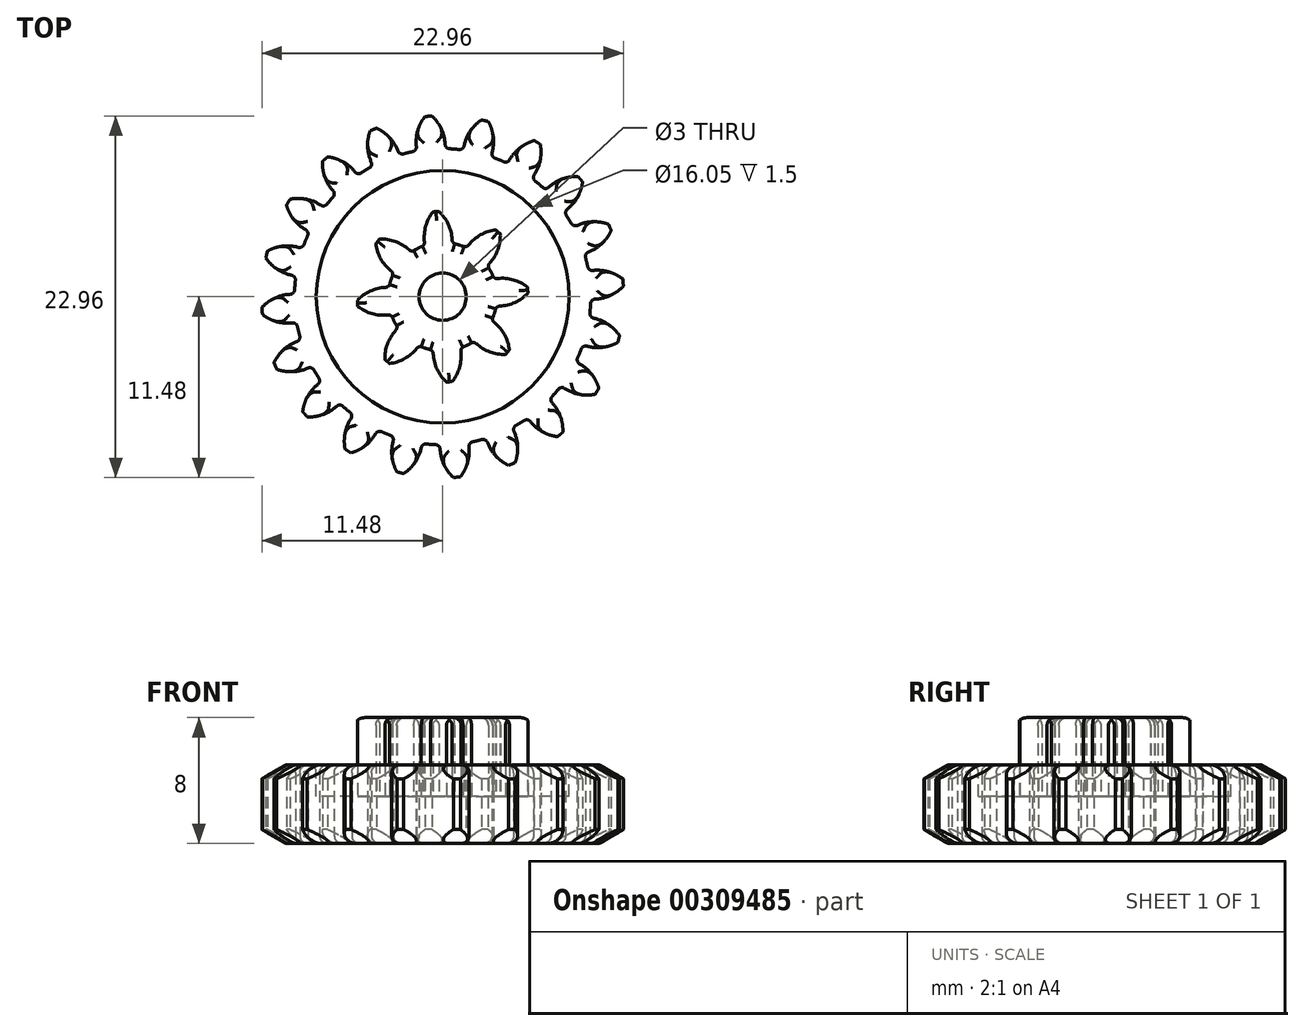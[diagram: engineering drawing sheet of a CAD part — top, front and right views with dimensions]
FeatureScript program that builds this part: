
annotation { "Feature Type Name" : "Feature", "Feature Type Description" : "" }
export const myFeature = defineFeature(function(context is Context, id is Id, definition is map)
    precondition{}
    {
        {
            assignVariable(context, id + "F0", {"name" : "GearDepth", "anyValue" : 5});
        }
        {
            var Q0;
            Q0=qCreatedBy(makeId("Top.planeOp"),FACE);
            var sketch = newSketch(context, id + "F1", { "sketchPlane" : qUnion([Q0])});
            skArc(sketch, "E0", {"start": v(-1.9, 9.21) * mm, "mid": v(0.74, -9.38) * mm, "end": v(0.44, 9.4) * mm});
            skCircle(sketch, "E1", {"center": v(0, 0) * mm, "radius": 10.45 * mm, "construction": true});
            skCircle(sketch, "E2", {"center": v(0, 0) * mm, "radius": 11.5 * mm, "construction": true});
            skLineSegment(sketch, "E3", {"start": v(0, 0) * mm, "end": v(0, 17.6) * mm, "construction": true});
            skLineSegment(sketch, "E4", {"start": v(0, 0) * mm, "end": v(-1.42, 18) * mm});
            skLineSegment(sketch, "E5", {"start": v(0, 10.45) * mm, "end": v(-10.54, 10.45) * mm, "construction": true});
            skLineSegment(sketch, "E6", {"start": v(0, 10.45) * mm, "end": v(-10.3, 6.7) * mm, "construction": true});
            skCircle(sketch, "E7", {"center": v(0, 10.45) * mm, "radius": 2.61 * mm, "construction": true});
            skCircle(sketch, "E8", {"center": v(-2.46, 9.56) * mm, "radius": 2.61 * mm, "construction": true});
            skArc(sketch, "E9", {"start": v(-4.91, 10.45) * mm, "mid": v(-4.92, 10.42) * mm, "end": v(-4.94, 10.39) * mm});
            skArc(sketch, "E10.trimOffspring", {"start": v(0.15, 9.68) * mm, "mid": v(-0.09, 10.66) * mm, "end": v(-0.68, 11.48) * mm});
            skArc(sketch, "E11.MirrorCS", {"start": v(-1.67, 9.54) * mm, "mid": v(-1.58, 10.55) * mm, "end": v(-1.12, 11.45) * mm});
            skLineSegment(sketch, "E12", {"start": v(-1.12, 11.45) * mm, "end": v(-0.68, 11.48) * mm});
            skCircle(sketch, "E13", {"center": v(0, 0) * mm, "radius": 1.5 * mm});
            skPoint(sketch, "E14.visualSharp", {"position": v(-1.62, 9.27) * mm});
            skArc(sketch, "E14.filletArc", {"start": v(-1.9, 9.21) * mm, "mid": v(-1.72, 9.33) * mm, "end": v(-1.67, 9.54) * mm});
            skPoint(sketch, "E15.visualSharp", {"position": v(0.15, 9.4) * mm});
            skArc(sketch, "E15.filletArc", {"start": v(0.15, 9.68) * mm, "mid": v(0.24, 9.49) * mm, "end": v(0.44, 9.4) * mm});
            skSolve(sketch);
        }
        {
            var Q0;
            {var subQ0=sQuery(id+"F1.wireOp",EDGE,"E10.trimOffspring");Q0=makeQuery(id+"F1.imprint","IMPRINT",FACE,{"disambiguationData":[TD([[makeQuery(id+"F1.imprint","IMPRINT",EDGE,{"derivedFrom":subQ0}),1.0]])]});}
            var Q1;
            {var subQ0=sQuery(id+"F1.wireOp",EDGE,"E0");var subQ1=makeQuery(id+"F1.imprint","INTERSECT",VERTEX,{"derivedFrom":[subQ0,sQuery(id+"F1.wireOp",EDGE,"E10.trimOffspring")]});Q1=makeQuery(id+"F1.imprint","IMPRINT",FACE,{"disambiguationData":[TD([[makeQuery(id+"F1.imprint","IMPRINT",EDGE,{"disambiguationData":[TD([[subQ1,-1.0]])],"derivedFrom":subQ0}),1.0]])]});}
            var Q2;
            {var subQ0=sQuery(id+"F1.wireOp",EDGE,"ff0f1e59-5a19-46eb-ac47-c6f22bc8a670.1.0");Q2=makeQuery(id+"F1.imprint","IMPRINT",FACE,{"disambiguationData":[TD([[makeQuery(id+"F1.imprint","IMPRINT",EDGE,{"derivedFrom":subQ0}),1.0]])]});}
            var Q3;
            {var subQ0=sQuery(id+"F1.wireOp",EDGE,"ff0f1e59-5a19-46eb-ac47-c6f22bc8a670.2.0");Q3=makeQuery(id+"F1.imprint","IMPRINT",FACE,{"disambiguationData":[TD([[makeQuery(id+"F1.imprint","IMPRINT",EDGE,{"derivedFrom":subQ0}),1.0]])]});}
            var Q4;
            {var subQ0=sQuery(id+"F1.wireOp",EDGE,"ff0f1e59-5a19-46eb-ac47-c6f22bc8a670.3.0");Q4=makeQuery(id+"F1.imprint","IMPRINT",FACE,{"disambiguationData":[TD([[makeQuery(id+"F1.imprint","IMPRINT",EDGE,{"derivedFrom":subQ0}),1.0]])]});}
            var Q5;
            {var subQ0=sQuery(id+"F1.wireOp",EDGE,"ff0f1e59-5a19-46eb-ac47-c6f22bc8a670.4.0");Q5=makeQuery(id+"F1.imprint","IMPRINT",FACE,{"disambiguationData":[TD([[makeQuery(id+"F1.imprint","IMPRINT",EDGE,{"derivedFrom":subQ0}),1.0]])]});}
            var Q6;
            {var subQ0=sQuery(id+"F1.wireOp",EDGE,"ff0f1e59-5a19-46eb-ac47-c6f22bc8a670.5.0");Q6=makeQuery(id+"F1.imprint","IMPRINT",FACE,{"disambiguationData":[TD([[makeQuery(id+"F1.imprint","IMPRINT",EDGE,{"derivedFrom":subQ0}),1.0]])]});}
            var Q7;
            {var subQ0=sQuery(id+"F1.wireOp",EDGE,"ff0f1e59-5a19-46eb-ac47-c6f22bc8a670.6.0");Q7=makeQuery(id+"F1.imprint","IMPRINT",FACE,{"disambiguationData":[TD([[makeQuery(id+"F1.imprint","IMPRINT",EDGE,{"derivedFrom":subQ0}),1.0]])]});}
            var Q8;
            {var subQ0=sQuery(id+"F1.wireOp",EDGE,"ff0f1e59-5a19-46eb-ac47-c6f22bc8a670.7.0");Q8=makeQuery(id+"F1.imprint","IMPRINT",FACE,{"disambiguationData":[TD([[makeQuery(id+"F1.imprint","IMPRINT",EDGE,{"derivedFrom":subQ0}),1.0]])]});}
            var Q9;
            {var subQ0=sQuery(id+"F1.wireOp",EDGE,"ff0f1e59-5a19-46eb-ac47-c6f22bc8a670.8.0");Q9=makeQuery(id+"F1.imprint","IMPRINT",FACE,{"disambiguationData":[TD([[makeQuery(id+"F1.imprint","IMPRINT",EDGE,{"derivedFrom":subQ0}),1.0]])]});}
            var Q10;
            {var subQ0=sQuery(id+"F1.wireOp",EDGE,"ff0f1e59-5a19-46eb-ac47-c6f22bc8a670.9.0");Q10=makeQuery(id+"F1.imprint","IMPRINT",FACE,{"disambiguationData":[TD([[makeQuery(id+"F1.imprint","IMPRINT",EDGE,{"derivedFrom":subQ0}),1.0]])]});}
            var Q11;
            {var subQ0=sQuery(id+"F1.wireOp",EDGE,"ff0f1e59-5a19-46eb-ac47-c6f22bc8a670.10.0");Q11=makeQuery(id+"F1.imprint","IMPRINT",FACE,{"disambiguationData":[TD([[makeQuery(id+"F1.imprint","IMPRINT",EDGE,{"derivedFrom":subQ0}),1.0]])]});}
            var Q12;
            {var subQ0=sQuery(id+"F1.wireOp",EDGE,"ff0f1e59-5a19-46eb-ac47-c6f22bc8a670.11.0");Q12=makeQuery(id+"F1.imprint","IMPRINT",FACE,{"disambiguationData":[TD([[makeQuery(id+"F1.imprint","IMPRINT",EDGE,{"derivedFrom":subQ0}),1.0]])]});}
            var Q13;
            {var subQ0=sQuery(id+"F1.wireOp",EDGE,"ff0f1e59-5a19-46eb-ac47-c6f22bc8a670.12.0");Q13=makeQuery(id+"F1.imprint","IMPRINT",FACE,{"disambiguationData":[TD([[makeQuery(id+"F1.imprint","IMPRINT",EDGE,{"derivedFrom":subQ0}),1.0]])]});}
            var Q14;
            {var subQ0=sQuery(id+"F1.wireOp",EDGE,"ff0f1e59-5a19-46eb-ac47-c6f22bc8a670.13.0");Q14=makeQuery(id+"F1.imprint","IMPRINT",FACE,{"disambiguationData":[TD([[makeQuery(id+"F1.imprint","IMPRINT",EDGE,{"derivedFrom":subQ0}),1.0]])]});}
            var Q15;
            {var subQ0=sQuery(id+"F1.wireOp",EDGE,"ff0f1e59-5a19-46eb-ac47-c6f22bc8a670.14.0");Q15=makeQuery(id+"F1.imprint","IMPRINT",FACE,{"disambiguationData":[TD([[makeQuery(id+"F1.imprint","IMPRINT",EDGE,{"derivedFrom":subQ0}),1.0]])]});}
            var Q16;
            {var subQ0=sQuery(id+"F1.wireOp",EDGE,"ff0f1e59-5a19-46eb-ac47-c6f22bc8a670.15.0");Q16=makeQuery(id+"F1.imprint","IMPRINT",FACE,{"disambiguationData":[TD([[makeQuery(id+"F1.imprint","IMPRINT",EDGE,{"derivedFrom":subQ0}),1.0]])]});}
            var Q17;
            {var subQ0=sQuery(id+"F1.wireOp",EDGE,"ff0f1e59-5a19-46eb-ac47-c6f22bc8a670.16.0");Q17=makeQuery(id+"F1.imprint","IMPRINT",FACE,{"disambiguationData":[TD([[makeQuery(id+"F1.imprint","IMPRINT",EDGE,{"derivedFrom":subQ0}),1.0]])]});}
            var Q18;
            {var subQ0=sQuery(id+"F1.wireOp",EDGE,"ff0f1e59-5a19-46eb-ac47-c6f22bc8a670.17.0");Q18=makeQuery(id+"F1.imprint","IMPRINT",FACE,{"disambiguationData":[TD([[makeQuery(id+"F1.imprint","IMPRINT",EDGE,{"derivedFrom":subQ0}),1.0]])]});}
            var Q19;
            {var subQ0=sQuery(id+"F1.wireOp",EDGE,"ff0f1e59-5a19-46eb-ac47-c6f22bc8a670.18.0");Q19=makeQuery(id+"F1.imprint","IMPRINT",FACE,{"disambiguationData":[TD([[makeQuery(id+"F1.imprint","IMPRINT",EDGE,{"derivedFrom":subQ0}),1.0]])]});}
            var Q20;
            {var subQ0=sQuery(id+"F1.wireOp",EDGE,"ff0f1e59-5a19-46eb-ac47-c6f22bc8a670.19.0");Q20=makeQuery(id+"F1.imprint","IMPRINT",FACE,{"disambiguationData":[TD([[makeQuery(id+"F1.imprint","IMPRINT",EDGE,{"derivedFrom":subQ0}),1.0]])]});}
            var Q21;
            Q21=sQuery(id+"F1.wireOp",EDGE,"E0");
            var Q22;
            Q22=sQuery(id+"F1.wireOp",EDGE,"E10.trimOffspring");
            var Q23;
            Q23=sQuery(id+"F1.wireOp",EDGE,"E12");
            var Q24;
            Q24=sQuery(id+"F1.wireOp",EDGE,"E11.MirrorCS");
            extrude(context, id + "F2", {"entities" : qUnion([Q0, Q1, Q2, Q3, Q4, Q5, Q6, Q7, Q8, Q9, Q10, Q11, Q12, Q13, Q14, Q15, Q16, Q17, Q18, Q19, Q20]), "surfaceEntities" : qUnion([Q21, Q22, Q23, Q24]), "depth" : (getVariable(context, 'GearDepth')) * mm});
        }
        {
            var Q0;
            Q0=makeQuery(id+"F2.opExtrude","SWEPT_BODY",BODY,{"disambiguationData":[OSD([sQuery(id+"F1.wireOp",EDGE,"E0"),sQuery(id+"F1.wireOp",EDGE,"E10.trimOffspring"),sQuery(id+"F1.wireOp",EDGE,"E11.MirrorCS"),sQuery(id+"F1.wireOp",EDGE,"E12"),sQuery(id+"F1.wireOp",EDGE,"E13"),sQuery(id+"F1.wireOp",EDGE,"E14.filletArc"),sQuery(id+"F1.wireOp",EDGE,"E15.filletArc")])]});
            var Q1;
            Q1=makeQuery(id+"F2.opExtrude","CAP_EDGE",EDGE,{"disambiguationData":[OSD([sQuery(id+"F1.wireOp",EDGE,"E13")])],"isStart":true});
            circularPattern(context, id + "F3", {"operationType" : NewBodyOperationType.ADD, "entities" : qUnion([Q0]), "axis" : qUnion([Q1]), "angle" : 360 * degree, "instanceCount" : 20, "equalSpace" : true});
        }
        {
            var Q0;
            Q0=qCreatedBy(makeId("Front.planeOp"),FACE);
            var sketch = newSketch(context, id + "F4", { "sketchPlane" : qUnion([Q0])});
            skLineSegment(sketch, "E16.0", {"start": v(11.48, 5) * mm, "end": v(11.48, 0) * mm});
            skLineSegment(sketch, "E17", {"start": v(11.48, 2.5) * mm, "end": v(14.42, 2.5) * mm, "construction": true});
            skLineSegment(sketch, "E18", {"start": v(8.27, 5.98) * mm, "end": v(12.07, 5.98) * mm});
            skLineSegment(sketch, "E19", {"start": v(12.07, 5.98) * mm, "end": v(12.07, 3.78) * mm});
            skLineSegment(sketch, "E20", {"start": v(12.07, 3.78) * mm, "end": v(8.27, 5.98) * mm});
            skLineSegment(sketch, "E21.MirrorCS", {"start": v(11.48, 0) * mm, "end": v(11.48, 5) * mm});
            skLineSegment(sketch, "E22.MirrorCS", {"start": v(8.27, -0.98) * mm, "end": v(12.07, -0.98) * mm});
            skLineSegment(sketch, "E23.MirrorCS", {"start": v(12.07, 1.22) * mm, "end": v(8.27, -0.98) * mm});
            skLineSegment(sketch, "E24.MirrorCS", {"start": v(12.07, -0.98) * mm, "end": v(12.07, 1.22) * mm});
            skSolve(sketch);
        }
        {
            var Q0;
            {var subQ0=sQuery(id+"F4.wireOp",EDGE,"E18");Q0=makeQuery(id+"F4.imprint","IMPRINT",FACE,{"disambiguationData":[TD([[makeQuery(id+"F4.imprint","IMPRINT",EDGE,{"derivedFrom":subQ0}),-1.0]])]});}
            var Q1;
            {var subQ0=sQuery(id+"F4.wireOp",EDGE,"E22.MirrorCS");Q1=makeQuery(id+"F4.imprint","IMPRINT",FACE,{"disambiguationData":[TD([[makeQuery(id+"F4.imprint","IMPRINT",EDGE,{"derivedFrom":subQ0}),1.0]])]});}
            var Q2;
            Q2=makeQuery(id+"F2.opExtrude","CAP_EDGE",EDGE,{"disambiguationData":[OSD([sQuery(id+"F1.wireOp",EDGE,"E13")])],"isStart":false});
            revolve(context, id + "F5", {"operationType" : NewBodyOperationType.REMOVE, "entities" : qUnion([Q0, Q1]), "axis" : qUnion([Q2]), "revolveType" : RevolveType.FULL, "oppositeDirection" : true});
        }
        {
            var Q0;
            {var subQ0=makeQuery(id+"F2.opExtrude","CAP_FACE",FACE,{"disambiguationData":[OSD([sQuery(id+"F1.wireOp",EDGE,"E0"),sQuery(id+"F1.wireOp",EDGE,"E10.trimOffspring"),sQuery(id+"F1.wireOp",EDGE,"E11.MirrorCS"),sQuery(id+"F1.wireOp",EDGE,"E12"),sQuery(id+"F1.wireOp",EDGE,"E13"),sQuery(id+"F1.wireOp",EDGE,"E14.filletArc"),sQuery(id+"F1.wireOp",EDGE,"E15.filletArc")])],"isStart":false});Q0=makeQuery(id+"F3.boolean.opBoolean","MERGE",FACE,{"derivedFrom":[subQ0,makeQuery(id+"F3.opPattern","COPY",FACE,{"derivedFrom":subQ0,"instanceName":"1"}),makeQuery(id+"F3.opPattern","COPY",FACE,{"derivedFrom":subQ0,"instanceName":"2"}),makeQuery(id+"F3.opPattern","COPY",FACE,{"derivedFrom":subQ0,"instanceName":"3"}),makeQuery(id+"F3.opPattern","COPY",FACE,{"derivedFrom":subQ0,"instanceName":"4"}),makeQuery(id+"F3.opPattern","COPY",FACE,{"derivedFrom":subQ0,"instanceName":"5"}),makeQuery(id+"F3.opPattern","COPY",FACE,{"derivedFrom":subQ0,"instanceName":"6"}),makeQuery(id+"F3.opPattern","COPY",FACE,{"derivedFrom":subQ0,"instanceName":"7"}),makeQuery(id+"F3.opPattern","COPY",FACE,{"derivedFrom":subQ0,"instanceName":"8"}),makeQuery(id+"F3.opPattern","COPY",FACE,{"derivedFrom":subQ0,"instanceName":"9"}),makeQuery(id+"F3.opPattern","COPY",FACE,{"derivedFrom":subQ0,"instanceName":"10"}),makeQuery(id+"F3.opPattern","COPY",FACE,{"derivedFrom":subQ0,"instanceName":"11"}),makeQuery(id+"F3.opPattern","COPY",FACE,{"derivedFrom":subQ0,"instanceName":"12"}),makeQuery(id+"F3.opPattern","COPY",FACE,{"derivedFrom":subQ0,"instanceName":"13"}),makeQuery(id+"F3.opPattern","COPY",FACE,{"derivedFrom":subQ0,"instanceName":"14"}),makeQuery(id+"F3.opPattern","COPY",FACE,{"derivedFrom":subQ0,"instanceName":"15"}),makeQuery(id+"F3.opPattern","COPY",FACE,{"derivedFrom":subQ0,"instanceName":"16"}),makeQuery(id+"F3.opPattern","COPY",FACE,{"derivedFrom":subQ0,"instanceName":"17"}),makeQuery(id+"F3.opPattern","COPY",FACE,{"derivedFrom":subQ0,"instanceName":"18"}),makeQuery(id+"F3.opPattern","COPY",FACE,{"derivedFrom":subQ0,"instanceName":"19"})]});}
            var sketch = newSketch(context, id + "F6", { "sketchPlane" : qUnion([Q0])});
            skCircle(sketch, "E25", {"center": v(0, 0) * mm, "radius": 8.02 * mm});
            skCircle(sketch, "E26", {"center": v(0, 0) * mm, "radius": 3.45 * mm});
            skSolve(sketch);
        }
        {
            var Q0;
            Q0=makeQuery(id+"F6.imprint","IMPRINT",FACE,{"disambiguationData":[TD([[makeQuery(id+"F6.imprint","IMPRINT",EDGE,{"derivedFrom":sQuery(id+"F6.wireOp",EDGE,"E25")}),1.0]])]});
            extrude(context, id + "F7", {"entities" : qUnion([Q0]), "operationType" : NewBodyOperationType.REMOVE, "oppositeDirection" : true, "depth" : 2 * mm});
        }
        {
            var Q0;
            {var subQ0=sQuery(id+"F1.wireOp",EDGE,"E13");var subQ1=makeQuery(id+"F2.opExtrude","CAP_FACE",FACE,{"disambiguationData":[OSD([sQuery(id+"F1.wireOp",EDGE,"E0"),sQuery(id+"F1.wireOp",EDGE,"E10.trimOffspring"),sQuery(id+"F1.wireOp",EDGE,"E11.MirrorCS"),sQuery(id+"F1.wireOp",EDGE,"E12"),subQ0,sQuery(id+"F1.wireOp",EDGE,"E14.filletArc"),sQuery(id+"F1.wireOp",EDGE,"E15.filletArc")])],"isStart":false});Q0=makeQuery(id+"F7.boolean.opBoolean","SPLIT",FACE,{"disambiguationData":[TD([makeQuery(id+"F2.opExtrude","SWEPT_FACE",FACE,{"disambiguationData":[OSD([subQ0])]})])],"derivedFrom":makeQuery(id+"F3.boolean.opBoolean","MERGE",FACE,{"derivedFrom":[subQ1,makeQuery(id+"F3.opPattern","COPY",FACE,{"derivedFrom":subQ1,"instanceName":"1"}),makeQuery(id+"F3.opPattern","COPY",FACE,{"derivedFrom":subQ1,"instanceName":"2"}),makeQuery(id+"F3.opPattern","COPY",FACE,{"derivedFrom":subQ1,"instanceName":"3"}),makeQuery(id+"F3.opPattern","COPY",FACE,{"derivedFrom":subQ1,"instanceName":"4"}),makeQuery(id+"F3.opPattern","COPY",FACE,{"derivedFrom":subQ1,"instanceName":"5"}),makeQuery(id+"F3.opPattern","COPY",FACE,{"derivedFrom":subQ1,"instanceName":"6"}),makeQuery(id+"F3.opPattern","COPY",FACE,{"derivedFrom":subQ1,"instanceName":"7"}),makeQuery(id+"F3.opPattern","COPY",FACE,{"derivedFrom":subQ1,"instanceName":"8"}),makeQuery(id+"F3.opPattern","COPY",FACE,{"derivedFrom":subQ1,"instanceName":"9"}),makeQuery(id+"F3.opPattern","COPY",FACE,{"derivedFrom":subQ1,"instanceName":"10"}),makeQuery(id+"F3.opPattern","COPY",FACE,{"derivedFrom":subQ1,"instanceName":"11"}),makeQuery(id+"F3.opPattern","COPY",FACE,{"derivedFrom":subQ1,"instanceName":"12"}),makeQuery(id+"F3.opPattern","COPY",FACE,{"derivedFrom":subQ1,"instanceName":"13"}),makeQuery(id+"F3.opPattern","COPY",FACE,{"derivedFrom":subQ1,"instanceName":"14"}),makeQuery(id+"F3.opPattern","COPY",FACE,{"derivedFrom":subQ1,"instanceName":"15"}),makeQuery(id+"F3.opPattern","COPY",FACE,{"derivedFrom":subQ1,"instanceName":"16"}),makeQuery(id+"F3.opPattern","COPY",FACE,{"derivedFrom":subQ1,"instanceName":"17"}),makeQuery(id+"F3.opPattern","COPY",FACE,{"derivedFrom":subQ1,"instanceName":"18"}),makeQuery(id+"F3.opPattern","COPY",FACE,{"derivedFrom":subQ1,"instanceName":"19"})]})});}
            var sketch = newSketch(context, id + "F8", { "sketchPlane" : qUnion([Q0])});
            skCircle(sketch, "E27.0", {"center": v(0, 0) * mm, "radius": 3.45 * mm});
            skCircle(sketch, "E27.1", {"center": v(0, 0) * mm, "radius": 1.5 * mm});
            skLineSegment(sketch, "E28", {"start": v(0.47, -5.95) * mm, "end": v(-0.95, 12.05) * mm, "construction": true});
            skArc(sketch, "E29.trimOffspring", {"start": v(0.6, 3.62) * mm, "mid": v(0.36, 4.6) * mm, "end": v(-0.24, 5.42) * mm});
            skArc(sketch, "E30.MirrorCS", {"start": v(-1.16, 3.48) * mm, "mid": v(-1.07, 4.5) * mm, "end": v(-0.61, 5.39) * mm});
            skLineSegment(sketch, "E31", {"start": v(-0.61, 5.39) * mm, "end": v(-0.24, 5.42) * mm});
            skArc(sketch, "E32.filletArc", {"start": v(-1.4, 3.16) * mm, "mid": v(-1.21, 3.28) * mm, "end": v(-1.16, 3.48) * mm});
            skArc(sketch, "E33.filletArc", {"start": v(0.6, 3.62) * mm, "mid": v(0.69, 3.42) * mm, "end": v(0.88, 3.34) * mm});
            skArc(sketch, "E34.1.0", {"start": v(-3.28, 1.65) * mm, "mid": v(-3.93, 2.42) * mm, "end": v(-4.24, 3.38) * mm});
            skArc(sketch, "E34.1.1", {"start": v(-2.14, 2.98) * mm, "mid": v(-3, 3.5) * mm, "end": v(-4, 3.66) * mm});
            skArc(sketch, "E34.1.2", {"start": v(-2.14, 2.98) * mm, "mid": v(-1.94, 2.9) * mm, "end": v(-1.73, 2.98) * mm});
            skLineSegment(sketch, "E34.1.3", {"start": v(-4.24, 3.38) * mm, "end": v(-4, 3.66) * mm});
            skArc(sketch, "E34.1.4", {"start": v(-3.22, 1.25) * mm, "mid": v(-3.17, 1.46) * mm, "end": v(-3.28, 1.65) * mm});
            skArc(sketch, "E34.2.0", {"start": v(-3.48, -1.16) * mm, "mid": v(-4.5, -1.07) * mm, "end": v(-5.39, -0.61) * mm});
            skArc(sketch, "E34.2.1", {"start": v(-3.62, 0.6) * mm, "mid": v(-4.6, 0.36) * mm, "end": v(-5.42, -0.24) * mm});
            skArc(sketch, "E34.2.2", {"start": v(-3.62, 0.6) * mm, "mid": v(-3.42, 0.69) * mm, "end": v(-3.34, 0.88) * mm});
            skLineSegment(sketch, "E34.2.3", {"start": v(-5.39, -0.61) * mm, "end": v(-5.42, -0.24) * mm});
            skArc(sketch, "E34.2.4", {"start": v(-3.16, -1.4) * mm, "mid": v(-3.28, -1.21) * mm, "end": v(-3.48, -1.16) * mm});
            skArc(sketch, "E34.3.0", {"start": v(-1.65, -3.28) * mm, "mid": v(-2.42, -3.93) * mm, "end": v(-3.38, -4.24) * mm});
            skArc(sketch, "E34.3.1", {"start": v(-2.98, -2.14) * mm, "mid": v(-3.5, -3) * mm, "end": v(-3.66, -4) * mm});
            skArc(sketch, "E34.3.2", {"start": v(-2.98, -2.14) * mm, "mid": v(-2.9, -1.94) * mm, "end": v(-2.98, -1.73) * mm});
            skLineSegment(sketch, "E34.3.3", {"start": v(-3.38, -4.24) * mm, "end": v(-3.66, -4) * mm});
            skArc(sketch, "E34.3.4", {"start": v(-1.25, -3.22) * mm, "mid": v(-1.46, -3.17) * mm, "end": v(-1.65, -3.28) * mm});
            skArc(sketch, "E34.4.0", {"start": v(1.16, -3.48) * mm, "mid": v(1.07, -4.5) * mm, "end": v(0.61, -5.39) * mm});
            skArc(sketch, "E34.4.1", {"start": v(-0.6, -3.62) * mm, "mid": v(-0.36, -4.6) * mm, "end": v(0.24, -5.42) * mm});
            skArc(sketch, "E34.4.2", {"start": v(-0.6, -3.62) * mm, "mid": v(-0.69, -3.42) * mm, "end": v(-0.88, -3.34) * mm});
            skLineSegment(sketch, "E34.4.3", {"start": v(0.61, -5.39) * mm, "end": v(0.24, -5.42) * mm});
            skArc(sketch, "E34.4.4", {"start": v(1.4, -3.16) * mm, "mid": v(1.21, -3.28) * mm, "end": v(1.16, -3.48) * mm});
            skArc(sketch, "E34.5.0", {"start": v(3.28, -1.65) * mm, "mid": v(3.93, -2.42) * mm, "end": v(4.24, -3.38) * mm});
            skArc(sketch, "E34.5.1", {"start": v(2.14, -2.98) * mm, "mid": v(3, -3.5) * mm, "end": v(4, -3.66) * mm});
            skArc(sketch, "E34.5.2", {"start": v(2.14, -2.98) * mm, "mid": v(1.94, -2.9) * mm, "end": v(1.73, -2.98) * mm});
            skLineSegment(sketch, "E34.5.3", {"start": v(4.24, -3.38) * mm, "end": v(4, -3.66) * mm});
            skArc(sketch, "E34.5.4", {"start": v(3.22, -1.25) * mm, "mid": v(3.17, -1.46) * mm, "end": v(3.28, -1.65) * mm});
            skArc(sketch, "E34.6.0", {"start": v(3.48, 1.16) * mm, "mid": v(4.5, 1.07) * mm, "end": v(5.39, 0.61) * mm});
            skArc(sketch, "E34.6.1", {"start": v(3.62, -0.6) * mm, "mid": v(4.6, -0.36) * mm, "end": v(5.42, 0.24) * mm});
            skArc(sketch, "E34.6.2", {"start": v(3.62, -0.6) * mm, "mid": v(3.42, -0.69) * mm, "end": v(3.34, -0.88) * mm});
            skLineSegment(sketch, "E34.6.3", {"start": v(5.39, 0.61) * mm, "end": v(5.42, 0.24) * mm});
            skArc(sketch, "E34.6.4", {"start": v(3.16, 1.4) * mm, "mid": v(3.28, 1.21) * mm, "end": v(3.48, 1.16) * mm});
            skArc(sketch, "E34.7.0", {"start": v(1.65, 3.28) * mm, "mid": v(2.42, 3.93) * mm, "end": v(3.38, 4.24) * mm});
            skArc(sketch, "E34.7.1", {"start": v(2.98, 2.14) * mm, "mid": v(3.5, 3) * mm, "end": v(3.66, 4) * mm});
            skArc(sketch, "E34.7.2", {"start": v(2.98, 2.14) * mm, "mid": v(2.9, 1.94) * mm, "end": v(2.98, 1.73) * mm});
            skLineSegment(sketch, "E34.7.3", {"start": v(3.38, 4.24) * mm, "end": v(3.66, 4) * mm});
            skArc(sketch, "E34.7.4", {"start": v(1.25, 3.22) * mm, "mid": v(1.46, 3.17) * mm, "end": v(1.65, 3.28) * mm});
            skSolve(sketch);
        }
        {
            var Q0;
            Q0 = qSketchRegion(id + "F8", true);
            extrude(context, id + "F9", {"entities" : qUnion([Q0]), "operationType" : NewBodyOperationType.ADD, "depth" : 3 * mm, "hasSecondDirection" : true, "secondDirectionOppositeDirection" : true, "secondDirectionDepth" : 3 * mm});
        }
        {
            var Q0;
            {var subQ0=sQuery(id+"F1.wireOp",EDGE,"E15.filletArc");var subQ1=sQuery(id+"F1.wireOp",EDGE,"E14.filletArc");var subQ2=sQuery(id+"F1.wireOp",EDGE,"E12");var subQ3=sQuery(id+"F1.wireOp",EDGE,"E11.MirrorCS");var subQ4=sQuery(id+"F1.wireOp",EDGE,"E10.trimOffspring");var subQ5=sQuery(id+"F1.wireOp",EDGE,"E0");var subQ6=makeQuery(id+"F2.opExtrude","CAP_FACE",FACE,{"disambiguationData":[OSD([subQ5,subQ4,subQ3,subQ2,sQuery(id+"F1.wireOp",EDGE,"E13"),subQ1,subQ0])],"isStart":false});var subQ7=makeQuery(id+"F3.opPattern","COPY",FACE,{"derivedFrom":subQ6,"instanceName":"18"});var subQ8=makeQuery(id+"F3.opPattern","COPY",FACE,{"derivedFrom":subQ6,"instanceName":"16"});var subQ9=makeQuery(id+"F3.opPattern","COPY",FACE,{"derivedFrom":subQ6,"instanceName":"15"});var subQ10=makeQuery(id+"F3.opPattern","COPY",FACE,{"derivedFrom":subQ6,"instanceName":"14"});var subQ11=makeQuery(id+"F3.opPattern","COPY",FACE,{"derivedFrom":subQ6,"instanceName":"13"});var subQ12=makeQuery(id+"F3.opPattern","COPY",FACE,{"derivedFrom":subQ6,"instanceName":"11"});var subQ13=makeQuery(id+"F3.opPattern","COPY",FACE,{"derivedFrom":subQ6,"instanceName":"10"});var subQ14=makeQuery(id+"F3.opPattern","COPY",FACE,{"derivedFrom":subQ6,"instanceName":"9"});var subQ15=makeQuery(id+"F3.opPattern","COPY",FACE,{"derivedFrom":subQ6,"instanceName":"8"});var subQ16=makeQuery(id+"F3.opPattern","COPY",FACE,{"derivedFrom":subQ6,"instanceName":"7"});var subQ17=makeQuery(id+"F3.opPattern","COPY",FACE,{"derivedFrom":subQ6,"instanceName":"3"});var subQ18=makeQuery(id+"F3.opPattern","COPY",FACE,{"derivedFrom":subQ6,"instanceName":"17"});var subQ21=makeQuery(id+"F3.opPattern","COPY",FACE,{"derivedFrom":subQ6,"instanceName":"1"});var subQ22=makeQuery(id+"F3.opPattern","COPY",FACE,{"derivedFrom":subQ6,"instanceName":"2"});var subQ23=makeQuery(id+"F3.opPattern","COPY",FACE,{"derivedFrom":subQ6,"instanceName":"4"});var subQ26=makeQuery(id+"F3.opPattern","COPY",FACE,{"derivedFrom":subQ6,"instanceName":"12"});var subQ28=makeQuery(id+"F3.opPattern","COPY",FACE,{"derivedFrom":subQ6,"instanceName":"5"});var subQ29=makeQuery(id+"F3.opPattern","COPY",FACE,{"derivedFrom":subQ6,"instanceName":"6"});var subQ30=makeQuery(id+"F3.opPattern","COPY",FACE,{"derivedFrom":subQ6,"instanceName":"19"});Q0=makeQuery(id+"F7.boolean.opBoolean","SPLIT",FACE,{"disambiguationData":[TD([makeQuery(id+"F2.opExtrude","SWEPT_FACE",FACE,{"disambiguationData":[OSD([subQ5])]})])],"derivedFrom":makeQuery(id+"F3.boolean.opBoolean","MERGE",FACE,{"derivedFrom":[subQ6,subQ21,subQ22,subQ17,subQ23,subQ28,subQ29,subQ16,subQ15,subQ14,subQ13,subQ12,subQ26,subQ11,subQ10,subQ9,subQ8,subQ18,subQ7,subQ30]})});}
            var Q1;
            {var subQ0=makeQuery(id+"F2.opExtrude","CAP_FACE",FACE,{"disambiguationData":[OSD([sQuery(id+"F1.wireOp",EDGE,"E0"),sQuery(id+"F1.wireOp",EDGE,"E10.trimOffspring"),sQuery(id+"F1.wireOp",EDGE,"E11.MirrorCS"),sQuery(id+"F1.wireOp",EDGE,"E12"),sQuery(id+"F1.wireOp",EDGE,"E13"),sQuery(id+"F1.wireOp",EDGE,"E14.filletArc"),sQuery(id+"F1.wireOp",EDGE,"E15.filletArc")])],"isStart":true});Q1=makeQuery(id+"F3.boolean.opBoolean","MERGE",FACE,{"derivedFrom":[subQ0,makeQuery(id+"F3.opPattern","COPY",FACE,{"derivedFrom":subQ0,"instanceName":"1"}),makeQuery(id+"F3.opPattern","COPY",FACE,{"derivedFrom":subQ0,"instanceName":"2"}),makeQuery(id+"F3.opPattern","COPY",FACE,{"derivedFrom":subQ0,"instanceName":"3"}),makeQuery(id+"F3.opPattern","COPY",FACE,{"derivedFrom":subQ0,"instanceName":"4"}),makeQuery(id+"F3.opPattern","COPY",FACE,{"derivedFrom":subQ0,"instanceName":"5"}),makeQuery(id+"F3.opPattern","COPY",FACE,{"derivedFrom":subQ0,"instanceName":"6"}),makeQuery(id+"F3.opPattern","COPY",FACE,{"derivedFrom":subQ0,"instanceName":"7"}),makeQuery(id+"F3.opPattern","COPY",FACE,{"derivedFrom":subQ0,"instanceName":"8"}),makeQuery(id+"F3.opPattern","COPY",FACE,{"derivedFrom":subQ0,"instanceName":"9"}),makeQuery(id+"F3.opPattern","COPY",FACE,{"derivedFrom":subQ0,"instanceName":"10"}),makeQuery(id+"F3.opPattern","COPY",FACE,{"derivedFrom":subQ0,"instanceName":"11"}),makeQuery(id+"F3.opPattern","COPY",FACE,{"derivedFrom":subQ0,"instanceName":"12"}),makeQuery(id+"F3.opPattern","COPY",FACE,{"derivedFrom":subQ0,"instanceName":"13"}),makeQuery(id+"F3.opPattern","COPY",FACE,{"derivedFrom":subQ0,"instanceName":"14"}),makeQuery(id+"F3.opPattern","COPY",FACE,{"derivedFrom":subQ0,"instanceName":"15"}),makeQuery(id+"F3.opPattern","COPY",FACE,{"derivedFrom":subQ0,"instanceName":"16"}),makeQuery(id+"F3.opPattern","COPY",FACE,{"derivedFrom":subQ0,"instanceName":"17"}),makeQuery(id+"F3.opPattern","COPY",FACE,{"derivedFrom":subQ0,"instanceName":"18"}),makeQuery(id+"F3.opPattern","COPY",FACE,{"derivedFrom":subQ0,"instanceName":"19"})]});}
            var Q2;
            Q2=makeQuery(id+"F9.opExtrude","CAP_FACE",FACE,{"disambiguationData":[OSD([sQuery(id+"F8.wireOp",EDGE,"E27.0"),sQuery(id+"F8.wireOp",EDGE,"E27.1"),sQuery(id+"F8.wireOp",EDGE,"E29.trimOffspring"),sQuery(id+"F8.wireOp",EDGE,"E30.MirrorCS"),sQuery(id+"F8.wireOp",EDGE,"E31"),sQuery(id+"F8.wireOp",EDGE,"E32.filletArc"),sQuery(id+"F8.wireOp",EDGE,"E33.filletArc"),sQuery(id+"F8.wireOp",EDGE,"E34.1.0"),sQuery(id+"F8.wireOp",EDGE,"E34.1.1"),sQuery(id+"F8.wireOp",EDGE,"E34.1.2"),sQuery(id+"F8.wireOp",EDGE,"E34.1.3"),sQuery(id+"F8.wireOp",EDGE,"E34.1.4"),sQuery(id+"F8.wireOp",EDGE,"E34.2.0"),sQuery(id+"F8.wireOp",EDGE,"E34.2.1"),sQuery(id+"F8.wireOp",EDGE,"E34.2.2"),sQuery(id+"F8.wireOp",EDGE,"E34.2.3"),sQuery(id+"F8.wireOp",EDGE,"E34.2.4"),sQuery(id+"F8.wireOp",EDGE,"E34.3.0"),sQuery(id+"F8.wireOp",EDGE,"E34.3.1"),sQuery(id+"F8.wireOp",EDGE,"E34.3.2"),sQuery(id+"F8.wireOp",EDGE,"E34.3.3"),sQuery(id+"F8.wireOp",EDGE,"E34.3.4"),sQuery(id+"F8.wireOp",EDGE,"E34.4.0"),sQuery(id+"F8.wireOp",EDGE,"E34.4.1"),sQuery(id+"F8.wireOp",EDGE,"E34.4.2"),sQuery(id+"F8.wireOp",EDGE,"E34.4.3"),sQuery(id+"F8.wireOp",EDGE,"E34.4.4"),sQuery(id+"F8.wireOp",EDGE,"E34.5.0"),sQuery(id+"F8.wireOp",EDGE,"E34.5.1"),sQuery(id+"F8.wireOp",EDGE,"E34.5.2"),sQuery(id+"F8.wireOp",EDGE,"E34.5.3"),sQuery(id+"F8.wireOp",EDGE,"E34.5.4"),sQuery(id+"F8.wireOp",EDGE,"E34.6.0"),sQuery(id+"F8.wireOp",EDGE,"E34.6.1"),sQuery(id+"F8.wireOp",EDGE,"E34.6.2"),sQuery(id+"F8.wireOp",EDGE,"E34.6.3"),sQuery(id+"F8.wireOp",EDGE,"E34.6.4"),sQuery(id+"F8.wireOp",EDGE,"E34.7.0"),sQuery(id+"F8.wireOp",EDGE,"E34.7.1"),sQuery(id+"F8.wireOp",EDGE,"E34.7.2"),sQuery(id+"F8.wireOp",EDGE,"E34.7.3"),sQuery(id+"F8.wireOp",EDGE,"E34.7.4")])],"isStart":false});
            fillet(context, id + "F10", {"entities" : qUnion([Q0, Q1, Q2]), "radius" : 0.5 * mm, "tangentPropagation" : true, "allowEdgeOverflow" : false});
        }
    });
